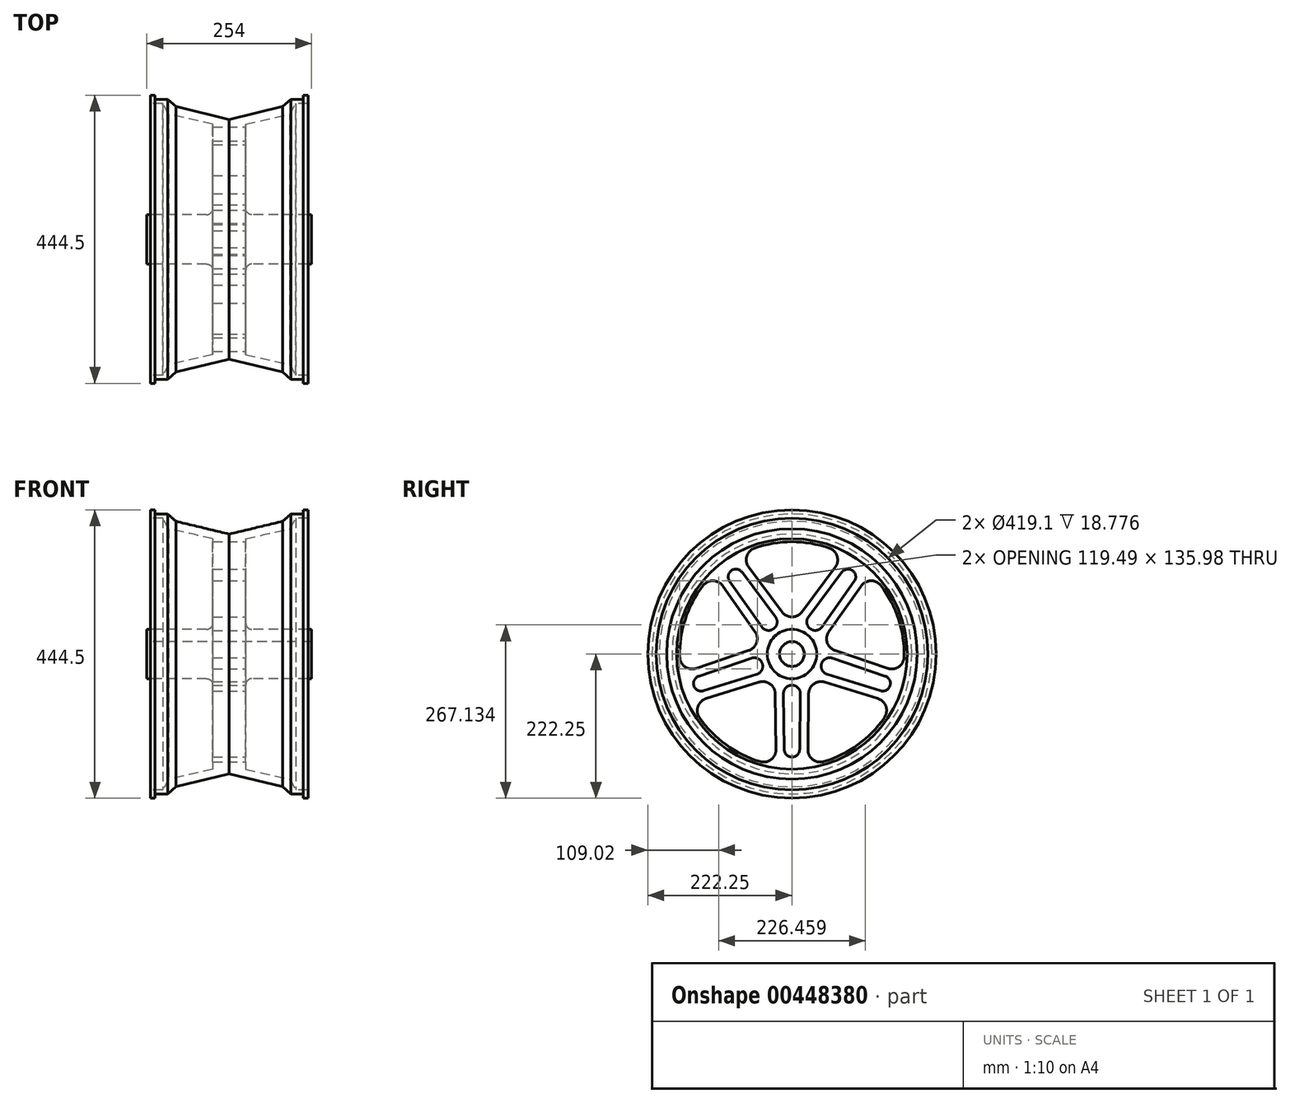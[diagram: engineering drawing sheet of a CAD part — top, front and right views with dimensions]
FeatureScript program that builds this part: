
annotation { "Feature Type Name" : "Feature", "Feature Type Description" : "" }
export const myFeature = defineFeature(function(context is Context, id is Id, definition is map)
    precondition{}
    {
        {
            var Q0;
            Q0=qCreatedBy(makeId("Top.planeOp"),FACE);
            var sketch = newSketch(context, id + "F0", { "sketchPlane" : qUnion([Q0])});
            skLineSegment(sketch, "E0.bottom", {"start": v(0, 0) * mm, "end": v(127, 0) * mm, "construction": true});
            skLineSegment(sketch, "E0.top", {"start": v(0, 222.25) * mm, "end": v(127, 222.25) * mm, "construction": true});
            skLineSegment(sketch, "E0.left", {"start": v(0, 0) * mm, "end": v(0, 222.25) * mm, "construction": true});
            skLineSegment(sketch, "E0.right", {"start": v(127, 0) * mm, "end": v(127, 222.25) * mm, "construction": true});
            skLineSegment(sketch, "E1", {"start": v(0, 19.05) * mm, "end": v(127, 19.05) * mm});
            skLineSegment(sketch, "E2", {"start": v(127, 19.05) * mm, "end": v(127, 38.1) * mm});
            skLineSegment(sketch, "E3", {"start": v(127, 38.1) * mm, "end": v(25.4, 38.1) * mm});
            skLineSegment(sketch, "E4", {"start": v(25.4, 38.1) * mm, "end": v(25.4, 177.8) * mm});
            skLineSegment(sketch, "E5", {"start": v(25.4, 177.8) * mm, "end": v(93.65, 193.12) * mm});
            skLineSegment(sketch, "E6", {"start": v(93.65, 193.12) * mm, "end": v(102.64, 209.55) * mm});
            skLineSegment(sketch, "E7", {"start": v(102.64, 209.55) * mm, "end": v(121.42, 209.55) * mm});
            skLineSegment(sketch, "E8", {"start": v(121.42, 209.55) * mm, "end": v(121.42, 222.25) * mm});
            skLineSegment(sketch, "E9", {"start": v(127, 222.25) * mm, "end": v(114.3, 222.25) * mm});
            skLineSegment(sketch, "E10", {"start": v(114.3, 222.25) * mm, "end": v(114.3, 215.9) * mm});
            skLineSegment(sketch, "E11", {"start": v(114.3, 215.9) * mm, "end": v(95.06, 215.9) * mm});
            skLineSegment(sketch, "E12", {"start": v(95.06, 215.9) * mm, "end": v(82.5, 204.78) * mm});
            skLineSegment(sketch, "E13", {"start": v(82.5, 204.78) * mm, "end": v(0, 184.87) * mm});
            skLineSegment(sketch, "E14.MirrorCS", {"start": v(-82.5, 204.78) * mm, "end": v(0, 184.87) * mm});
            skLineSegment(sketch, "E15.MirrorCS", {"start": v(-95.06, 215.9) * mm, "end": v(-82.5, 204.78) * mm});
            skLineSegment(sketch, "E16.MirrorCS", {"start": v(-114.3, 215.9) * mm, "end": v(-95.06, 215.9) * mm});
            skLineSegment(sketch, "E17.MirrorCS", {"start": v(-114.3, 222.25) * mm, "end": v(-114.3, 215.9) * mm});
            skLineSegment(sketch, "E18.MirrorCS", {"start": v(-121.42, 222.25) * mm, "end": v(-114.3, 222.25) * mm});
            skLineSegment(sketch, "E19.MirrorCS", {"start": v(-121.42, 209.55) * mm, "end": v(-121.42, 222.25) * mm});
            skLineSegment(sketch, "E20.MirrorCS", {"start": v(-102.64, 209.55) * mm, "end": v(-121.42, 209.55) * mm});
            skLineSegment(sketch, "E21.MirrorCS", {"start": v(-93.65, 193.12) * mm, "end": v(-102.64, 209.55) * mm});
            skLineSegment(sketch, "E22.MirrorCS", {"start": v(-25.4, 177.8) * mm, "end": v(-93.65, 193.12) * mm});
            skLineSegment(sketch, "E23.MirrorCS", {"start": v(-25.4, 38.1) * mm, "end": v(-25.4, 177.8) * mm});
            skLineSegment(sketch, "E24.MirrorCS", {"start": v(-127, 38.1) * mm, "end": v(-25.4, 38.1) * mm});
            skLineSegment(sketch, "E25.MirrorCS", {"start": v(-127, 19.05) * mm, "end": v(-127, 38.1) * mm});
            skLineSegment(sketch, "E26.MirrorCS", {"start": v(0, 19.05) * mm, "end": v(-127, 19.05) * mm});
            skPoint(sketch, "E27.orphan", {"position": v(-127, 222.25) * mm});
            skSolve(sketch);
        }
        {
            var Q0;
            Q0 = qSketchRegion(id + "F0", true);
            var Q1;
            Q1=sQuery(id+"F0.wireOp",EDGE,"E0.bottom");
            revolve(context, id + "F1", {"entities" : qUnion([Q0]), "axis" : qUnion([Q1]), "revolveType" : RevolveType.FULL});
        }
        {
            var Q0;
            Q0=makeQuery(id+"F1.opRevolve","SWEPT_FACE",FACE,{"disambiguationData":[OSD([sQuery(id+"F0.wireOp",EDGE,"E4")])]});
            var sketch = newSketch(context, id + "F2", { "sketchPlane" : qUnion([Q0])});
            skLineSegment(sketch, "E28", {"start": v(0, 0) * mm, "end": v(0, 199.44) * mm, "construction": true});
            skLineSegment(sketch, "E29", {"start": v(0, 0) * mm, "end": v(182.48, 0) * mm, "construction": true});
            skArc(sketch, "E30", {"start": v(57.87, 163.07) * mm, "mid": v(0, 173.04) * mm, "end": v(-57.87, 163.07) * mm});
            skArc(sketch, "E31", {"start": v(-15.26, 64.8) * mm, "mid": v(0, 57.15) * mm, "end": v(15.26, 64.8) * mm});
            skArc(sketch, "E32", {"start": v(66.76, 133.72) * mm, "mid": v(69.73, 150.64) * mm, "end": v(57.87, 163.07) * mm});
            skArc(sketch, "E33", {"start": v(-57.87, 163.07) * mm, "mid": v(-69.73, 150.64) * mm, "end": v(-66.76, 133.72) * mm});
            skLineSegment(sketch, "E34", {"start": v(-66.76, 133.72) * mm, "end": v(-15.26, 64.8) * mm});
            skLineSegment(sketch, "E35", {"start": v(15.26, 64.8) * mm, "end": v(66.76, 133.72) * mm});
            skLineSegment(sketch, "E36.1.0", {"start": v(-147.8, -22.17) * mm, "end": v(-66.34, 5.51) * mm});
            skArc(sketch, "E36.1.1", {"start": v(-172.98, -4.65) * mm, "mid": v(-164.82, -19.77) * mm, "end": v(-147.8, -22.17) * mm});
            skArc(sketch, "E36.1.2", {"start": v(-137.2, 105.43) * mm, "mid": v(-164.57, 53.47) * mm, "end": v(-172.98, -4.65) * mm});
            skArc(sketch, "E36.1.3", {"start": v(-106.54, 104.82) * mm, "mid": v(-121.72, 112.87) * mm, "end": v(-137.2, 105.43) * mm});
            skLineSegment(sketch, "E36.1.4", {"start": v(-56.9, 34.54) * mm, "end": v(-106.54, 104.82) * mm});
            skArc(sketch, "E36.1.5", {"start": v(-66.34, 5.51) * mm, "mid": v(-54.35, 17.66) * mm, "end": v(-56.9, 34.54) * mm});
            skLineSegment(sketch, "E36.2.0", {"start": v(-24.58, -147.42) * mm, "end": v(-25.74, -61.4) * mm});
            skArc(sketch, "E36.2.1", {"start": v(-49.03, -165.95) * mm, "mid": v(-32.13, -162.86) * mm, "end": v(-24.58, -147.42) * mm});
            skArc(sketch, "E36.2.2", {"start": v(-142.67, -97.91) * mm, "mid": v(-101.7, -140) * mm, "end": v(-49.03, -165.95) * mm});
            skArc(sketch, "E36.2.3", {"start": v(-132.6, -68.94) * mm, "mid": v(-144.96, -80.88) * mm, "end": v(-142.67, -97.91) * mm});
            skLineSegment(sketch, "E36.2.4", {"start": v(-50.43, -43.45) * mm, "end": v(-132.6, -68.94) * mm});
            skArc(sketch, "E36.2.5", {"start": v(-25.74, -61.4) * mm, "mid": v(-33.6, -46.24) * mm, "end": v(-50.43, -43.45) * mm});
            skLineSegment(sketch, "E36.3.0", {"start": v(132.6, -68.94) * mm, "end": v(50.43, -43.45) * mm});
            skArc(sketch, "E36.3.1", {"start": v(142.67, -97.91) * mm, "mid": v(144.96, -80.88) * mm, "end": v(132.6, -68.94) * mm});
            skArc(sketch, "E36.3.2", {"start": v(49.03, -165.95) * mm, "mid": v(101.7, -140) * mm, "end": v(142.67, -97.91) * mm});
            skArc(sketch, "E36.3.3", {"start": v(24.58, -147.42) * mm, "mid": v(32.13, -162.86) * mm, "end": v(49.03, -165.95) * mm});
            skLineSegment(sketch, "E36.3.4", {"start": v(25.74, -61.4) * mm, "end": v(24.58, -147.42) * mm});
            skArc(sketch, "E36.3.5", {"start": v(50.43, -43.45) * mm, "mid": v(33.6, -46.24) * mm, "end": v(25.74, -61.4) * mm});
            skLineSegment(sketch, "E36.4.0", {"start": v(106.54, 104.82) * mm, "end": v(56.9, 34.54) * mm});
            skArc(sketch, "E36.4.1", {"start": v(137.2, 105.43) * mm, "mid": v(121.72, 112.87) * mm, "end": v(106.54, 104.82) * mm});
            skArc(sketch, "E36.4.2", {"start": v(172.98, -4.65) * mm, "mid": v(164.57, 53.47) * mm, "end": v(137.2, 105.43) * mm});
            skArc(sketch, "E36.4.3", {"start": v(147.8, -22.17) * mm, "mid": v(164.82, -19.77) * mm, "end": v(172.98, -4.65) * mm});
            skLineSegment(sketch, "E36.4.4", {"start": v(66.34, 5.51) * mm, "end": v(147.8, -22.17) * mm});
            skArc(sketch, "E36.4.5", {"start": v(56.9, 34.54) * mm, "mid": v(54.35, 17.66) * mm, "end": v(66.34, 5.51) * mm});
            skArc(sketch, "E37.trimOffspring", {"start": v(57.15, 0) * mm, "mid": v(56.45, 8.94) * mm, "end": v(54.35, 17.66) * mm});
            skSolve(sketch);
        }
        {
            var Q0;
            Q0 = qSketchRegion(id + "F2", true);
            extrude(context, id + "F3", {"entities" : qUnion([Q0]), "operationType" : NewBodyOperationType.REMOVE, "endBound" : BoundingType.THROUGH_ALL, "oppositeDirection" : true, "depth" : 25.4 * mm});
        }
        {
            var Q0;
            Q0=makeQuery(id+"F1.opRevolve","SWEPT_FACE",FACE,{"disambiguationData":[OSD([sQuery(id+"F0.wireOp",EDGE,"E4")])]});
            var sketch = newSketch(context, id + "F4", { "sketchPlane" : qUnion([Q0])});
            skLineSegment(sketch, "E38.0", {"start": v(25.43, 57.2) * mm, "end": v(76.94, 126.11) * mm});
            skLineSegment(sketch, "E39.0", {"start": v(96.17, 112.14) * mm, "end": v(46.54, 41.86) * mm});
            skArc(sketch, "E40", {"start": v(76.94, 126.11) * mm, "mid": v(93.44, 128.61) * mm, "end": v(96.17, 112.14) * mm});
            skArc(sketch, "E41", {"start": v(46.54, 41.86) * mm, "mid": v(28.21, 38.83) * mm, "end": v(25.43, 57.2) * mm});
            skLineSegment(sketch, "E42.1.0", {"start": v(-76.94, 126.11) * mm, "end": v(-25.43, 57.2) * mm});
            skArc(sketch, "E42.1.1", {"start": v(-96.17, 112.14) * mm, "mid": v(-93.44, 128.61) * mm, "end": v(-76.94, 126.11) * mm});
            skLineSegment(sketch, "E42.1.2", {"start": v(-46.54, 41.86) * mm, "end": v(-96.17, 112.14) * mm});
            skArc(sketch, "E42.1.3", {"start": v(-25.43, 57.2) * mm, "mid": v(-28.21, 38.83) * mm, "end": v(-46.54, 41.86) * mm});
            skLineSegment(sketch, "E42.2.0", {"start": v(-143.72, -34.2) * mm, "end": v(-62.25, -6.51) * mm});
            skArc(sketch, "E42.2.1", {"start": v(-136.37, -56.8) * mm, "mid": v(-151.2, -49.13) * mm, "end": v(-143.72, -34.2) * mm});
            skLineSegment(sketch, "E42.2.2", {"start": v(-54.2, -31.32) * mm, "end": v(-136.37, -56.8) * mm});
            skArc(sketch, "E42.2.3", {"start": v(-62.25, -6.51) * mm, "mid": v(-45.65, -14.83) * mm, "end": v(-54.2, -31.32) * mm});
            skLineSegment(sketch, "E42.3.0", {"start": v(-11.89, -147.25) * mm, "end": v(-13.04, -61.22) * mm});
            skArc(sketch, "E42.3.1", {"start": v(11.89, -147.25) * mm, "mid": v(0, -158.98) * mm, "end": v(-11.89, -147.25) * mm});
            skLineSegment(sketch, "E42.3.2", {"start": v(13.04, -61.22) * mm, "end": v(11.89, -147.25) * mm});
            skArc(sketch, "E42.3.3", {"start": v(-13.04, -61.22) * mm, "mid": v(0, -48) * mm, "end": v(13.04, -61.22) * mm});
            skLineSegment(sketch, "E42.4.0", {"start": v(136.37, -56.8) * mm, "end": v(54.2, -31.32) * mm});
            skArc(sketch, "E42.4.1", {"start": v(143.72, -34.2) * mm, "mid": v(151.2, -49.13) * mm, "end": v(136.37, -56.8) * mm});
            skLineSegment(sketch, "E42.4.2", {"start": v(62.25, -6.51) * mm, "end": v(143.72, -34.2) * mm});
            skArc(sketch, "E42.4.3", {"start": v(54.2, -31.32) * mm, "mid": v(45.65, -14.83) * mm, "end": v(62.25, -6.51) * mm});
            skPoint(sketch, "E42.center", {"position": v(0, 0) * mm});
            skSolve(sketch);
        }
        {
            var Q0;
            Q0 = qSketchRegion(id + "F4", true);
            extrude(context, id + "F5", {"entities" : qUnion([Q0]), "operationType" : NewBodyOperationType.REMOVE, "endBound" : BoundingType.THROUGH_ALL, "oppositeDirection" : true, "depth" : 25.4 * mm});
        }
        {
            var Q0;
            Q0=makeQuery(id+"F1.opRevolve","SWEPT_EDGE",EDGE,{"disambiguationData":[OSD([sQuery(id+"F0.wireOp",EDGE,"E3"),sQuery(id+"F0.wireOp",EDGE,"E4")])]});
            var Q1;
            Q1=makeQuery(id+"F1.opRevolve","SWEPT_EDGE",EDGE,{"disambiguationData":[OSD([sQuery(id+"F0.wireOp",EDGE,"E23.MirrorCS"),sQuery(id+"F0.wireOp",EDGE,"E24.MirrorCS")])]});
            fillet(context, id + "F6", {"entities" : qUnion([Q0, Q1]), "radius" : 9.52 * mm, "tangentPropagation" : true, "allowEdgeOverflow" : false});
        }
    });
